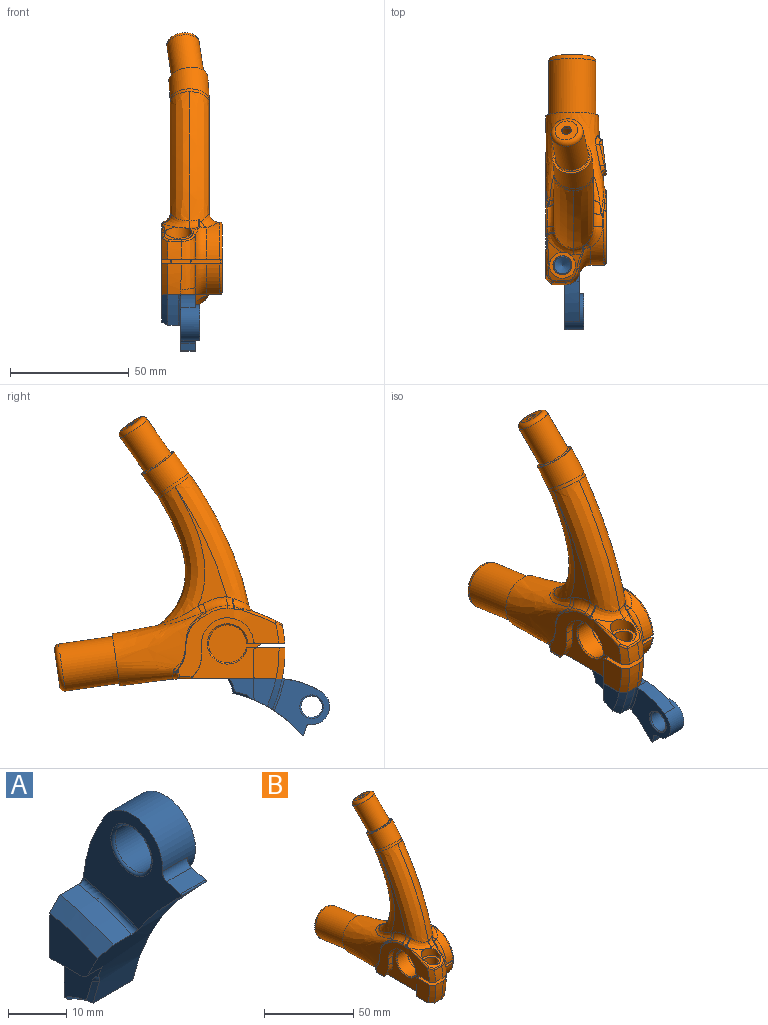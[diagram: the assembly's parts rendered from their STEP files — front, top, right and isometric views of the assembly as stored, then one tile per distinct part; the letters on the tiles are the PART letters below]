
ASSEMBLY  parts=2 mates=1
PART A: 30 faces, bbox 16x26.3x43 mm
  f0: cone r=1.92mm half-angle=30deg, axis (0,-1,0), area 16mm2, adj f3,f14
  f1: torus R=5mm, axis (1,0,0), area 23.1mm2, adj f6,f22
  f2: torus R=5mm, axis (1,0,0), area 23.1mm2, adj f6,f21
  f3: cylinder r=2.5mm len=5mm, axis (0,-1,0), area 23.6mm2, adj f0,f11
  f4: cylinder r=3.5mm len=8mm, axis (0,1,0), area 175.9mm2, adj f5,f11
  f5: cone r=3.5mm half-angle=59deg, axis (0,1,0), area 44.9mm2, adj f4
  f6: cylinder r=4.5mm len=9mm, axis (-1,0,0), area 197.9mm2, adj f1,f2
  f7: cylinder r=7.5mm len=15mm, axis (-1,0,0), area 214.8mm2, adj f9,f12,f15,f21,f22
  f8: cylinder r=54.2mm len=26.91mm, axis (1,0,0), area 287.8mm2, adj f9,f10,f16,f17,f19,f20,f22,f23
  f9: plane 39.51x23.84mm, normal (1,0,0), area 357.8mm2, adj f7,f8,f10,f11,f12,f13,f15,f16
  f10: cylinder r=13mm len=9.5mm, axis (1,0,0), area 61.7mm2, adj f8,f9,f11,f27
  f11: plane 22.95x14mm, normal (0,1,0), area 221mm2, adj f3,f4,f9,f10,f15,f17,f18,f20
  f12: cylinder r=1.5mm len=6mm, axis (-1,0,0), area 12.6mm2, adj f7,f9,f13,f22
  f13: plane 6x3.33mm, normal (0,-0.27,0.96), area 20.7mm2, adj f9,f12,f22,f24
  f14: plane 3.85x3.85mm, normal (0,1,0), area 11.6mm2, adj f0
  f15: cylinder r=35.51mm len=16.56mm, axis (1,0,0), area 106.2mm2, adj f7,f9,f11,f22,f29
  f16: plane 6x2.58mm, normal (0,-0.72,-0.69), area 21.5mm2, adj f8,f9,f22,f24
  f17: plane 10.99x9.23mm, normal (-1,0,0), area 58.4mm2, adj f8,f11,f18,f19,f26,f27,f28
  f18: plane 7.24x3.5mm, normal (0,0,-1), area 25.3mm2, adj f11,f17,f19,f20
  f19: cylinder r=2.5mm len=3.5mm, axis (-1,0,0), area 8.1mm2, adj f8,f17,f18,f20
  f20: plane 11.61x9.41mm, normal (-1,0,0), area 81.5mm2, adj f8,f11,f18,f19,f25
  f21: plane 15x15mm, normal (1,0,0), area 98.2mm2, adj f2,f7
  f22: plane 23.75x23.25mm, normal (-1,0,0), area 259.8mm2, adj f1,f7,f8,f12,f13,f15,f16,f24
  f23: cylinder r=63.91mm len=12.89mm, axis (-1,0,0), area 61mm2, adj f8,f11,f25,f29
  f24: cylinder r=0.25mm len=6mm, axis (-1,0,0), area 3.1mm2, adj f9,f13,f16,f22
  f25: revolved ~12.89x6.55mm, area 45.3mm2, adj f8,f11,f20,f23
  f26: revolved ~1.92x1.82mm, area 1.3mm2, adj f8,f17,f28
  f27: revolved ~6.49x3.17mm, area 8mm2, adj f10,f11,f17,f28
  f28: bspline ~5.46x2.14mm, area 6.7mm2, adj f8,f17,f26,f27
  f29: torus R=64.91mm, axis (1,0,0), area 21.6mm2, adj f8,f15,f22,f23
PART B: 268 faces, bbox 34.1x103.6x122.7 mm
  f0: bspline ~49.29x25.08mm, area 63.3mm2, adj f4,f5,f6,f7,f8,f9,f10,f11
  f1: cylinder r=2.4mm len=2.22mm, axis (1,0,0), area 0.6mm2, adj f12,f13,f264
  f2: cylinder r=2.4mm len=2.18mm, axis (1,0,0), area 2.1mm2, adj f3,f12,f263
  f3: plane 8.83x2.39mm, normal (0,0.14,0.99), area 7.7mm2, adj f2,f12,f248,f261
  f4: plane 4.04x2.12mm, normal (0,0.14,0.99), area 6.5mm2, adj f0,f5,f12,f251
  f5: cylinder r=1.2mm len=1.78mm, axis (1,0,0), area 3mm2, adj f0,f4,f6,f12
  f6: plane 3.57x1.51mm, normal (0,0.99,-0.14), area 5.1mm2, adj f0,f5,f7,f12
  f7: plane 3.57x1.82mm, normal (0,0.14,0.99), area 5mm2, adj f0,f6,f8,f12
  f8: cylinder r=1.2mm len=1.56mm, axis (1,0,0), area 2.7mm2, adj f0,f7,f9,f12
  f9: plane 3.96x1.65mm, normal (0,0.99,-0.14), area 6.1mm2, adj f0,f8,f10,f12
  f10: cylinder r=1.2mm len=1.95mm, axis (1,0,0), area 3.2mm2, adj f0,f9,f11,f12
  f11: plane 8.77x3mm, normal (0,-0.14,-0.99), area 16.4mm2, adj f0,f10,f12,f250
  f12: plane 14.86x14.81mm, normal (0.99,0.12,-0.02), area 79.9mm2, adj f1,f2,f3,f4,f5,f6,f7,f8
  f13: plane 8.78x1.56mm, normal (0,-0.14,-0.99), area 2.2mm2, adj f1,f12,f247,f260,f262
  f14: bspline ~37.93x9.69mm, area 0mm2, adj f0,f15,f17
  f15: plane 3.17x1.58mm, normal (0,0.99,-0.14), area 4.4mm2, adj f0,f14,f16,f17,f18
  f16: plane 8.42x4.27mm, normal (0.99,0.12,-0.02), area 26mm2, adj f15,f17,f18,f254
  f17: plane 8.15x2.25mm, normal (0,-0.14,-0.99), area 11.1mm2, adj f0,f14,f15,f16,f254
  f18: plane 8.18x2.57mm, normal (0,0.14,0.99), area 13.1mm2, adj f0,f15,f16,f254
  f19: bspline ~46.72x33.05mm, area 2027.9mm2, adj f134,f142,f143,f144,f145,f146,f147,f161
  f20: bspline ~38.52x8.69mm, area 0.2mm2, adj f0,f23,f24,f253
  f21: plane 3.43x1.83mm, normal (0,-0.14,-0.99), area 4.8mm2, adj f0,f22,f24,f252
  f22: plane 3.67x3.62mm, normal (0.99,0.12,-0.02), area 10.5mm2, adj f21,f23,f24,f252
  f23: plane 3.41x1.65mm, normal (0,0.14,0.99), area 4.3mm2, adj f0,f20,f22,f24,f252,f253
  f24: plane 3.21x1.45mm, normal (0,0.99,-0.14), area 4.2mm2, adj f0,f20,f21,f22,f23
  f25: plane 10.63x8.07mm, normal (-1,0,0), area 36.8mm2, adj f80,f82,f109,f110,f111,f123,f236
  f26: cylinder r=9mm len=24.33mm, axis (0,-0.99,0.14), area 1244.1mm2, adj f28,f30
  f27: plane 16x15.84mm, normal (0,-0.99,0.14), area 181.4mm2, adj f28,f32
  f28: torus R=8mm, axis (0,0.99,-0.14), area 85.2mm2, adj f26,f27
  f29: plane 16x15.84mm, normal (0,0.99,-0.14), area 181.4mm2, adj f30,f31
  f30: torus R=8mm, axis (0,0.99,-0.14), area 85.2mm2, adj f26,f29
  f31: cylinder r=2.5mm len=5.11mm, axis (0,0.99,-0.14), area 17.3mm2, adj f29,f77
  f32: cylinder r=2.5mm len=5.09mm, axis (0,0.99,-0.14), area 15.7mm2, adj f27,f232
  f33: plane 10.3x5.05mm, normal (0,0,-1), area 6.2mm2, adj f46,f48,f94,f124
  f34: plane 12.22x5.03mm, normal (0,0,1), area 7.4mm2, adj f81,f83,f85,f91,f112
  f35: plane 2.28x1.15mm, normal (0,0,1), area 1.1mm2, adj f81,f86,f112
  f36: plane 26.95x9.3mm, normal (0,0,1), area 120.1mm2, adj f46,f54,f68,f78,f88,f110,f113,f114
  f37: plane 2.28x1.15mm, normal (0,0,-1), area 1.1mm2, adj f81,f86,f120
  f38: bspline ~4.27x2.58mm, area 0.4mm2, adj f39,f42,f95
  f39: torus R=19.88mm, axis (1,0,0), area 29.8mm2, adj f38,f40,f42,f73
  f40: bspline ~9.94x8.15mm, area 32.1mm2, adj f39,f42,f43,f71
  f41: bspline ~3.54x3.01mm, area 0.8mm2, adj f42,f78,f105
  f42: cylinder r=15.45mm len=30.84mm, axis (1,0,0), area 602.9mm2, adj f38,f39,f40,f41,f43,f44,f45,f46
  f43: bspline ~7.28x5.79mm, area 6.9mm2, adj f40,f42,f44,f71,f99
  f44: torus R=20.88mm, axis (1,0,0), area 56.8mm2, adj f42,f43,f45,f48,f56,f59,f60,f90
  f45: plane 12.58x8.47mm, normal (0,0,-1), area 7.9mm2, adj f42,f44,f47,f48,f87,f90,f94,f108
  f46: plane 29.35x29.09mm, normal (-1,0,0), area 246.9mm2, adj f33,f36,f42,f48,f54,f78,f104,f107
  f47: cylinder r=6.6mm len=2.04mm, axis (0,0,1), area 0mm2, adj f45,f90
  f48: cylinder r=6.6mm len=12.5mm, axis (0,0,1), area 80.5mm2, adj f33,f42,f44,f45,f46,f51,f60,f94
  f49: plane 15.22x8.03mm, normal (0,0,-1), area 25.9mm2, adj f81,f82,f83,f85,f89,f92,f120
  f50: cylinder r=64.75mm len=3.26mm, axis (1,0,0), area 3.4mm2, adj f61,f87,f94,f108
  f51: cylinder r=64.75mm len=7.93mm, axis (1,0,0), area 18mm2, adj f48,f94,f101
  f52: plane 4.8x0.51mm, normal (0,0,1), area 0.8mm2, adj f93,f121,f126,f127,f237
  f53: plane 2.42x1.27mm, normal (0,0,1), area 1mm2, adj f58,f94,f116,f122
  f54: cylinder r=14.78mm len=2.5mm, axis (-1,0,0), area 3.1mm2, adj f36,f46,f88,f104
  f55: plane 10.98x7.69mm, normal (0,0,1), area 23.7mm2, adj f82,f89,f110,f112,f113
  f56: plane 3.15x0.5mm, normal (0,0,1), area 1.3mm2, adj f42,f44,f59,f122
  f57: plane 4.25x2.5mm, normal (0,1,0), area 10.6mm2, adj f58,f62,f93,f118
  f58: cylinder r=12.1mm len=24.12mm, axis (1,0,0), area 89.8mm2, adj f53,f57,f93,f107,f116,f122
  f59: plane 14.48x7.19mm, normal (0,0,1), area 22.3mm2, adj f44,f56,f61,f87,f90,f94,f122
  f60: cylinder r=64.75mm len=3.7mm, axis (1,0,0), area 4.6mm2, adj f44,f48,f99,f101
  f61: cone r=51.92mm half-angle=45deg, axis (1,0,0), area 18mm2, adj f50,f59,f87,f94
  f62: extruded ~9x3.5mm, area 25mm2, adj f57,f93,f113,f115,f119
  f63: bspline ~6.19x4.11mm, area 3.2mm2, adj f64,f78,f94,f100
  f64: bspline ~12.03x7.04mm, area 6.3mm2, adj f63,f78,f94
  f65: bspline ~3.49x3mm, area 0mm2, adj f78,f94
  f66: bspline ~11.99x7.93mm, area 7.8mm2, adj f67,f78,f94
  f67: bspline ~3.32x3.05mm, area 0.7mm2, adj f66,f68,f78,f94
  f68: bspline ~9.26x5.91mm, area 12.3mm2, adj f36,f67,f78,f94,f114
  f69: bspline ~65.62x19.25mm, area 638.4mm2, adj f70,f71,f73,f76,f96
  f70: bspline ~66.46x19.74mm, area 646.7mm2, adj f69,f72,f74,f76,f97
  f71: bspline ~58.25x31.28mm, area 635.8mm2, adj f40,f43,f69,f72,f73,f76,f99
  f72: bspline ~58.25x31.28mm, area 633.7mm2, adj f70,f71,f74,f76,f101,f102,f103
  f73: plane 48.91x21.71mm, normal (-1,0,0), area 174.5mm2, adj f39,f69,f71,f95
  f74: plane 49.88x21.73mm, normal (1,0,0), area 177.2mm2, adj f70,f72,f98,f100
  f75: torus R=100mm, axis (0,0.82,-0.58), area 361.3mm2, adj f76,f131
  f76: cylinder r=7.15mm len=14.3mm, axis (0,-0.58,-0.82), area 66.2mm2, adj f69,f70,f71,f72,f75
  f77: plane 18.02x17.83mm, normal (0,-0.99,0.14), area 240.9mm2, adj f31,f132
  f78: offset ~52.73x35.63mm, area 1923.4mm2, adj f36,f41,f42,f46,f63,f64,f65,f66
  f79: cylinder r=9.1mm len=18.2mm, axis (-1,0,0), area 195.6mm2, adj f125,f126,f127,f236
  f80: plane 6.81x2.35mm, normal (0,0,-1), area 5.9mm2, adj f25,f93,f123,f125,f127,f236
  f81: plane 10.8x9.16mm, normal (1,0,0), area 95.1mm2, adj f34,f35,f37,f49,f85,f86,f112,f120
  f82: cylinder r=15.45mm len=10.8mm, axis (1,0,0), area 63.8mm2, adj f25,f49,f55,f89,f109,f110,f120
  f83: cylinder r=51.6mm len=10.8mm, axis (-1,0,0), area 56.1mm2, adj f34,f49,f85,f91,f92
  f84: plane 2.21x1.64mm, normal (-1,0,0), area 1.3mm2, adj f89,f91,f112
  f85: cone r=51.92mm half-angle=45deg, axis (1,0,0), area 28.5mm2, adj f34,f49,f81,f83
  f86: plane 11.06x2.78mm, normal (0,-1,0), area 26.7mm2, adj f35,f37,f81,f109,f112,f120
  f87: cylinder r=51.6mm len=6.18mm, axis (1,0,0), area 32.1mm2, adj f45,f50,f59,f61,f90,f108
  f88: plane 15.55x0.9mm, normal (-1,0,0), area 7.9mm2, adj f36,f54,f78,f104
  f89: torus R=20.88mm, axis (1,0,0), area 79.8mm2, adj f49,f55,f82,f84,f92,f112
  f90: bspline ~9.92x5.21mm, area 37.8mm2, adj f44,f45,f47,f59,f87
  f91: torus R=46.7mm, axis (1,0,0), area 14.1mm2, adj f34,f83,f84,f92,f112
  f92: bspline ~12.51x6mm, area 65.2mm2, adj f49,f83,f89,f91
  f93: plane 26.63x24.86mm, normal (1,0,0), area 204.8mm2, adj f52,f57,f58,f62,f80,f107,f109,f113
  f94: plane 42.32x28mm, normal (1,0,0), area 215.9mm2, adj f33,f45,f48,f50,f51,f53,f59,f61
  f95: bspline ~8.79x6.86mm, area 34.7mm2, adj f38,f42,f73,f78,f96
  f96: bspline ~21.35x11.8mm, area 86.9mm2, adj f69,f78,f95,f97
  f97: bspline ~20.99x10.82mm, area 74.6mm2, adj f70,f78,f96,f98
  f98: bspline ~8.07x6.64mm, area 11.3mm2, adj f74,f78,f97,f100
  f99: bspline ~8.75x4.85mm, area 19.5mm2, adj f43,f44,f60,f71,f101
  f100: torus R=19.84mm, axis (1,0,0), area 61.2mm2, adj f63,f74,f78,f94,f98,f102
  f101: bspline ~13.5x9.91mm, area 66.8mm2, adj f48,f51,f60,f72,f94,f99,f103
  f102: bspline ~5.62x5.26mm, area 13.6mm2, adj f72,f94,f100,f103
  f103: bspline ~5.44x5.17mm, area 2.7mm2, adj f72,f94,f101,f102
  f104: bspline ~6.72x1.66mm, area 4.1mm2, adj f46,f54,f78,f88
  f105: bspline ~24.55x8.66mm, area 49.4mm2, adj f41,f42,f78,f106
  f106: bspline ~3.2x2.53mm, area 0.3mm2, adj f42,f78,f105
  f107: cylinder r=5.1mm len=10.2mm, axis (0,0,-1), area 115.3mm2, adj f42,f46,f58,f93,f121,f122,f124,f237
  f108: cylinder r=6.6mm len=3.45mm, axis (0,0,1), area 5.4mm2, adj f45,f50,f87,f94
  f109: cylinder r=5.1mm len=10.2mm, axis (0,0,-1), area 268.1mm2, adj f25,f82,f86,f93,f112,f120,f123
  f110: cylinder r=3.65mm len=7.3mm, axis (0,0,-1), area 72.8mm2, adj f25,f36,f46,f55,f82,f111,f113,f236
  f111: plane 7.4x6.65mm, normal (0,0,1), area 39.5mm2, adj f25,f110,f236
  f112: torus R=6.1mm, axis (0,0,1), area 49.3mm2, adj f34,f35,f55,f81,f84,f86,f89,f91
  f113: cylinder r=1mm len=27.78mm, axis (0,-1,0), area 39mm2, adj f36,f55,f62,f93,f110,f112,f115
  f114: cylinder r=1mm len=4.04mm, axis (0,1,0), area 6.3mm2, adj f36,f68,f94,f117
  f115: cylinder r=1mm len=3.5mm, axis (1,0,0), area 2.7mm2, adj f36,f62,f113,f117
  f116: torus R=13.1mm, axis (-1,0,0), area 59.3mm2, adj f53,f58,f94,f118
  f117: sphere r=1mm, area 1mm2, adj f114,f115,f119
  f118: cylinder r=1mm len=4.25mm, axis (0,0,1), area 6.7mm2, adj f57,f94,f116,f119
  f119: bspline ~11.33x4.93mm, area 15.2mm2, adj f62,f94,f117,f118
  f120: torus R=6.1mm, axis (0,0,-1), area 34.4mm2, adj f37,f49,f81,f82,f86,f109
  f121: torus R=6.1mm, axis (0,0,-1), area 9.5mm2, adj f52,f93,f107,f237
  f122: bspline ~12.2x11.52mm, area 34.8mm2, adj f42,f53,f56,f58,f59,f94,f107
  f123: torus R=6.1mm, axis (0,0,-1), area 11.7mm2, adj f25,f80,f93,f109
  f124: torus R=6.1mm, axis (0,0,1), area 51.3mm2, adj f33,f42,f45,f46,f94,f107
  f125: cylinder r=1mm len=6.24mm, axis (-1,0,0), area 5.9mm2, adj f79,f80,f127,f236
  f126: cylinder r=1mm len=4.78mm, axis (-1,0,0), area 5.7mm2, adj f52,f79,f127,f238
  f127: torus R=10.1mm, axis (1,0,0), area 86mm2, adj f52,f79,f80,f93,f125,f126
  f128: plane 9.63x7.97mm, normal (0.12,-0.57,-0.81), area 61.3mm2, adj f129,f235
  f129: torus R=4.85mm, axis (-0.12,0.57,0.81), area 48.2mm2, adj f128,f130
  f130: cylinder r=5.75mm len=22.24mm, axis (0.12,-0.57,-0.81), area 690.8mm2, adj f129,f131
  f131: bspline ~14.2x12.06mm, area 105.9mm2, adj f75,f130
  f132: bspline ~20x19.79mm, area 92.8mm2, adj f77,f78
  f133: cylinder r=15.88mm len=14.4mm, axis (-1,0,0), area 23.1mm2, adj f134,f177,f197,f204
  f134: plane 47.28x25.57mm, normal (0,0,-1), area 514.1mm2, adj f19,f133,f141,f147,f165,f167,f172,f173
  f135: plane 25.41x7.89mm, normal (0,0,-1), area 79.1mm2, adj f138,f162,f163,f166,f168,f170,f183,f184
  f136: plane 4.25x3.5mm, normal (0,-1,0), area 14.9mm2, adj f137,f141,f183,f184
  f137: cylinder r=11mm len=21.94mm, axis (1,0,0), area 116.8mm2, adj f136,f183,f184,f244
  f138: plane 19.15x8.38mm, normal (0,0,-1), area 85.7mm2, adj f135,f140,f176,f178,f180,f184,f226
  f139: cylinder r=65.85mm len=17.45mm, axis (1,0,0), area 66.2mm2, adj f192,f194,f215,f216,f217,f218,f220,f228
  f140: cone r=52.7mm half-angle=45deg, axis (1,0,0), area 29mm2, adj f138,f176,f184,f215,f216
  f141: extruded ~10.45x4.4mm, area 40.2mm2, adj f134,f136,f183,f184,f225
  f142: bspline ~5.95x4.21mm, area 2.2mm2, adj f19,f143,f193,f210,f211
  f143: bspline ~13.89x7.81mm, area 4.2mm2, adj f19,f142,f184,f209
  f144: bspline ~3.33x2.05mm, area 0mm2, adj f19,f184
  f145: bspline ~11.88x7mm, area 5.8mm2, adj f19,f146,f222
  f146: bspline ~2.16x2.13mm, area 0.7mm2, adj f19,f145,f147,f223
  f147: bspline ~9.17x5.41mm, area 12.1mm2, adj f19,f134,f146,f224,f225
  f148: bspline ~65.62x20.07mm, area 723.5mm2, adj f149,f150,f152,f159,f187
  f149: bspline ~66.46x20.68mm, area 733.3mm2, adj f148,f151,f153,f159,f189
  f150: bspline ~58.89x32.37mm, area 737.4mm2, adj f148,f151,f152,f159,f188,f190,f192
  f151: bspline ~58.89x32.37mm, area 735mm2, adj f149,f150,f153,f159,f194,f195,f196
  f152: plane 48.91x21.71mm, normal (1,0,0), area 174.5mm2, adj f148,f150,f185,f186
  f153: plane 49.88x21.73mm, normal (-1,0,0), area 177.2mm2, adj f149,f151,f191,f193
  f154: cylinder r=6.85mm len=22.23mm, axis (0.12,-0.57,-0.81), area 754.3mm2, adj f156,f160
  f155: plane 9.63x7.97mm, normal (-0.12,0.57,0.81), area 61.3mm2, adj f156,f235
  f156: torus R=4.85mm, axis (-0.12,0.57,0.81), area 120.9mm2, adj f154,f155
  f157: plane 16.42x13.58mm, normal (-0.12,0.57,0.81), area 44mm2, adj f158,f160
  f158: torus R=100mm, axis (0,0.82,-0.58), area 572.7mm2, adj f157,f159
  f159: cylinder r=8.25mm len=16.5mm, axis (0,-0.58,-0.82), area 76.1mm2, adj f148,f149,f150,f151,f158
  f160: bspline ~14.58x12.05mm, area 31.7mm2, adj f154,f157
  f161: plane 22.2x21.98mm, normal (0,0.99,-0.14), area 72.9mm2, adj f19,f234
  f162: cylinder r=15.88mm len=22.93mm, axis (-1,0,0), area 106.1mm2, adj f135,f178,f186,f188,f199,f208
  f163: cylinder r=8mm len=16mm, axis (-1,0,0), area 386mm2, adj f135,f164,f242,f243
  f164: plane 25.53x16.51mm, normal (0,0,1), area 167.7mm2, adj f163,f165,f166,f167,f168,f169,f172,f174
  f165: cylinder r=15.88mm len=13mm, axis (-1,0,0), area 92.3mm2, adj f134,f164,f179,f202
  f166: plane 30.28x28.58mm, normal (1,0,0), area 15.1mm2, adj f135,f164,f202,f203,f204,f205,f206,f207
  f167: plane 13x10.72mm, normal (-1,0,0), area 133.8mm2, adj f134,f164,f174,f175,f245,f246
  f168: plane 28.7x27.53mm, normal (1,0,0), area 399.2mm2, adj f135,f164,f169,f170,f171,f242
  f169: cylinder r=14.35mm len=12.4mm, axis (1,0,0), area 185.9mm2, adj f164,f168,f171,f241
  f170: cylinder r=14.35mm len=28.7mm, axis (1,0,0), area 762.3mm2, adj f135,f168,f171,f239
  f171: plane 12.4x11.37mm, normal (0,0,1), area 141mm2, adj f168,f169,f170,f240
  f172: cylinder r=52.7mm len=13mm, axis (-1,0,0), area 73.7mm2, adj f134,f164,f174,f181,f182
  f173: plane 3.32x2.68mm, normal (1,0,0), area 3mm2, adj f134,f179,f181
  f174: cone r=52.7mm half-angle=45deg, axis (1,0,0), area 46.3mm2, adj f134,f164,f167,f172
  f175: plane 11x3.5mm, normal (0,1,0), area 38.5mm2, adj f167,f183,f245,f246
  f176: cylinder r=52.7mm len=7.56mm, axis (1,0,0), area 44.4mm2, adj f138,f140,f180,f216,f217
  f177: plane 15.04x1.06mm, normal (1,0,0), area 7.3mm2, adj f19,f133,f134,f197
  f178: torus R=20.88mm, axis (1,0,0), area 97.6mm2, adj f138,f162,f180,f190,f220,f221
  f179: torus R=20.88mm, axis (1,0,0), area 116mm2, adj f134,f164,f165,f173,f182
  f180: bspline ~15.1x8.01mm, area 72.6mm2, adj f138,f176,f178,f218
  f181: torus R=46.7mm, axis (1,0,0), area 27.6mm2, adj f134,f172,f173,f182
  f182: bspline ~14.94x7.14mm, area 90mm2, adj f164,f172,f179,f181
  f183: plane 27.81x26.11mm, normal (-1,0,0), area 295.7mm2, adj f134,f135,f136,f137,f141,f164,f175,f243
  f184: plane 44.03x30.63mm, normal (-1,0,0), area 364.9mm2, adj f19,f135,f136,f137,f138,f140,f141,f143
  f185: bspline ~8.54x5.9mm, area 29.5mm2, adj f19,f152,f187,f201
  f186: torus R=19.88mm, axis (1,0,0), area 35mm2, adj f152,f162,f188,f200,f201
  f187: bspline ~21.27x12.11mm, area 70.2mm2, adj f19,f148,f185,f189
  f188: bspline ~11.11x8.01mm, area 49.5mm2, adj f150,f162,f186,f190
  f189: bspline ~20.9x11.42mm, area 60.4mm2, adj f19,f149,f187,f191
  f190: bspline ~5.96x4.76mm, area 6.9mm2, adj f150,f178,f188,f219
  f191: bspline ~7.75x5.82mm, area 8.7mm2, adj f19,f153,f189,f193
  f192: bspline ~8.75x4.32mm, area 16.6mm2, adj f139,f150,f194,f219,f221
  f193: torus R=19.84mm, axis (1,0,0), area 50mm2, adj f19,f142,f153,f191,f195,f211
  f194: bspline ~13.5x9.8mm, area 59.8mm2, adj f139,f151,f192,f196,f213,f214,f228
  f195: bspline ~4.5x4.31mm, area 12.4mm2, adj f151,f193,f196,f212
  f196: bspline ~4.44x4.16mm, area 2.5mm2, adj f151,f194,f195,f213
  f197: bspline ~18.02x3.98mm, area 17.5mm2, adj f19,f133,f177,f198,f205
  f198: bspline ~26.23x8.19mm, area 41.8mm2, adj f19,f197,f199,f206
  f199: bspline ~5.95x3.39mm, area 4.8mm2, adj f19,f162,f198,f200,f207
  f200: bspline ~1.64x1.21mm, area 0.3mm2, adj f19,f186,f199,f201
  f201: bspline ~3.78x3.26mm, area 0.3mm2, adj f185,f186,f200
  f202: torus R=14.88mm, axis (1,0,0), area 26mm2, adj f164,f165,f166,f203
  f203: cylinder r=1mm len=11.99mm, axis (0,-1,0), area 18.5mm2, adj f134,f166,f202,f204
  f204: torus R=14.88mm, axis (1,0,0), area 4.1mm2, adj f133,f166,f203,f205
  f205: bspline ~4.1x3.09mm, area 2.5mm2, adj f166,f197,f204,f206
  f206: bspline ~25.59x7.33mm, area 24.2mm2, adj f166,f198,f205,f207
  f207: bspline ~5.9x4.25mm, area 5.2mm2, adj f166,f199,f206,f208
  f208: torus R=14.88mm, axis (1,0,0), area 49mm2, adj f135,f162,f166,f207
  f209: bspline ~12.29x7.39mm, area 3.8mm2, adj f143,f184,f210
  f210: bspline ~5.2x3.81mm, area 3.6mm2, adj f142,f184,f209,f211
  f211: torus R=15.07mm, axis (1,0,0), area 12mm2, adj f142,f184,f193,f210,f212
  f212: bspline ~4.06x1.32mm, area 3.4mm2, adj f184,f195,f211,f213
  f213: bspline ~2.72x1.56mm, area 0.8mm2, adj f184,f194,f196,f212,f214
  f214: bspline ~4.2x1.86mm, area 1.6mm2, adj f184,f194,f213
  f215: torus R=64.85mm, axis (-1,0,0), area -0.5mm2, adj f139,f140,f184,f216
  f216: bspline ~14.66x12.8mm, area 3.9mm2, adj f139,f140,f176,f215,f217
  f217: cylinder r=1mm len=5.74mm, axis (1,0,0), area 4.7mm2, adj f139,f176,f216,f218
  f218: bspline ~7.58x6.98mm, area 9.5mm2, adj f139,f180,f217,f220
  f219: bspline ~2.77x1.86mm, area 0.7mm2, adj f190,f192,f221
  f220: bspline ~10.41x4.61mm, area 7.8mm2, adj f139,f178,f218,f221
  f221: bspline ~3.29x2.02mm, area 1.5mm2, adj f178,f192,f219,f220
  f222: bspline ~10.9x3.73mm, area 1.3mm2, adj f145,f184,f223
  f223: bspline ~0.86x0.75mm, area 0.3mm2, adj f146,f184,f222,f224
  f224: bspline ~4.05x1.66mm, area 2.6mm2, adj f147,f184,f223,f225
  f225: cylinder r=1mm len=6.46mm, axis (0,1,0), area 8.8mm2, adj f134,f141,f147,f184,f224
  f226: cylinder r=4mm len=8mm, axis (0,0,-1), area 201.1mm2, adj f135,f138,f227
  f227: plane 11x11mm, normal (0,0,1), area 44.8mm2, adj f226,f228
  f228: cylinder r=5.5mm len=11mm, axis (0,0,1), area 112.2mm2, adj f139,f194,f227
  f229: cylinder r=4mm len=13mm, axis (0,0,-1), area 326.7mm2, adj f134,f164
  f230: cylinder r=2.55mm len=5.1mm, axis (0,0,-1), area 64.1mm2, adj f134,f231
  f231: plane 5.1x5.1mm, normal (0,0,-1), area 20.4mm2, adj f230
  f232: plane 16x15.84mm, normal (0,0.99,-0.14), area 181.4mm2, adj f32,f233
  f233: torus R=8mm, axis (0,0.99,-0.14), area 183mm2, adj f232,f234
  f234: cylinder r=10mm len=25.6mm, axis (0,-0.99,0.14), area 1445.1mm2, adj f161,f233
  f235: cylinder r=2mm len=4.11mm, axis (-0.12,0.57,0.81), area 13.8mm2, adj f128,f155
  f236: torus R=11.1mm, axis (1,0,0), area 175.1mm2, adj f25,f46,f79,f80,f110,f111,f125,f238
  f237: cylinder r=2mm len=3.54mm, axis (0,1,0), area 6.1mm2, adj f46,f52,f107,f121,f238
  f238: bspline ~2x2mm, area 1.8mm2, adj f126,f236,f237
  f239: cone r=14.35mm half-angle=45deg, axis (1,0,0), area 44.3mm2, adj f135,f166,f170,f240
  f240: plane 11.58x0.5mm, normal (0.71,0,0.71), area 8.1mm2, adj f166,f171,f239,f241
  f241: cone r=14.35mm half-angle=45deg, axis (1,0,0), area 10.8mm2, adj f164,f166,f169,f240
  f242: cone r=8mm half-angle=45deg, axis (1,0,0), area 35.2mm2, adj f135,f163,f164,f168
  f243: cone r=8.5mm half-angle=45deg, axis (-1,0,0), area 35.2mm2, adj f135,f163,f164,f183
  f244: cylinder r=1mm len=3.5mm, axis (1,0,0), area 5.1mm2, adj f135,f137,f183,f184
  f245: cylinder r=1mm len=3.5mm, axis (-1,0,0), area 5.5mm2, adj f164,f167,f175,f183
  f246: cylinder r=1mm len=3.5mm, axis (1,0,0), area 5.5mm2, adj f134,f167,f175,f183
  f247: extruded ~0.53x0.14mm, area 0mm2, adj f12,f13,f258
  f248: extruded ~1.74x0.64mm, area 0.4mm2, adj f3,f12,f259
  f249: plane 8.74x1.61mm, normal (0.12,-0.98,0.14), area 11.3mm2, adj f0,f12,f250,f251
  f250: extruded ~2.06x1.39mm, area 3.4mm2, adj f0,f11,f12,f249
  f251: extruded ~1.75x1.55mm, area 2.9mm2, adj f0,f4,f12,f249
  f252: plane 3.19x1.45mm, normal (0.12,-0.98,0.14), area 4.4mm2, adj f0,f21,f22,f23
  f253: plane 1.54x0.25mm, normal (-0.12,0.98,-0.14), area 0mm2, adj f0,f20,f23
  f254: plane 3.2x1.59mm, normal (0.12,-0.98,0.14), area 4.8mm2, adj f0,f16,f17,f18
  f255: bspline ~10.8x3.57mm, area 22.6mm2, adj f12,f19,f256,f257
  f256: bspline ~5.35x3.77mm, area 11.4mm2, adj f12,f19,f255,f258
  f257: bspline ~3.89x3.64mm, area 7.2mm2, adj f12,f19,f255,f259
  f258: bspline ~2.24x2.2mm, area 2mm2, adj f19,f247,f256,f260
  f259: bspline ~4.02x2.73mm, area 6.2mm2, adj f19,f248,f257,f261
  f260: bspline ~1.99x1.57mm, area 0.6mm2, adj f13,f19,f258,f262
  f261: bspline ~14.88x4.65mm, area 19.7mm2, adj f3,f19,f259,f263
  f262: bspline ~17.79x4.52mm, area 21.5mm2, adj f13,f19,f260,f264
  f263: bspline ~4.26x3.97mm, area 9.5mm2, adj f2,f19,f261,f265
  f264: bspline ~5.3x2.43mm, area 7.9mm2, adj f1,f19,f262,f266
  f265: bspline ~1.9x1.76mm, area 1.7mm2, adj f12,f19,f263,f267
  f266: bspline ~2.29x1.91mm, area 4mm2, adj f12,f19,f264,f267
  f267: bspline ~10.37x3.14mm, area 19.7mm2, adj f12,f19,f265,f266
PLACE A rot(axis=(1,0,0),90deg) t=(-158.14,-118.13,-45.71)mm
PLACE B t=(-237.14,300.94,-105.71)mm
MATE fastened A.f0 <-> B.f110  axis (0,0,1) through (-158.14,-124.08,-60.41)mm
